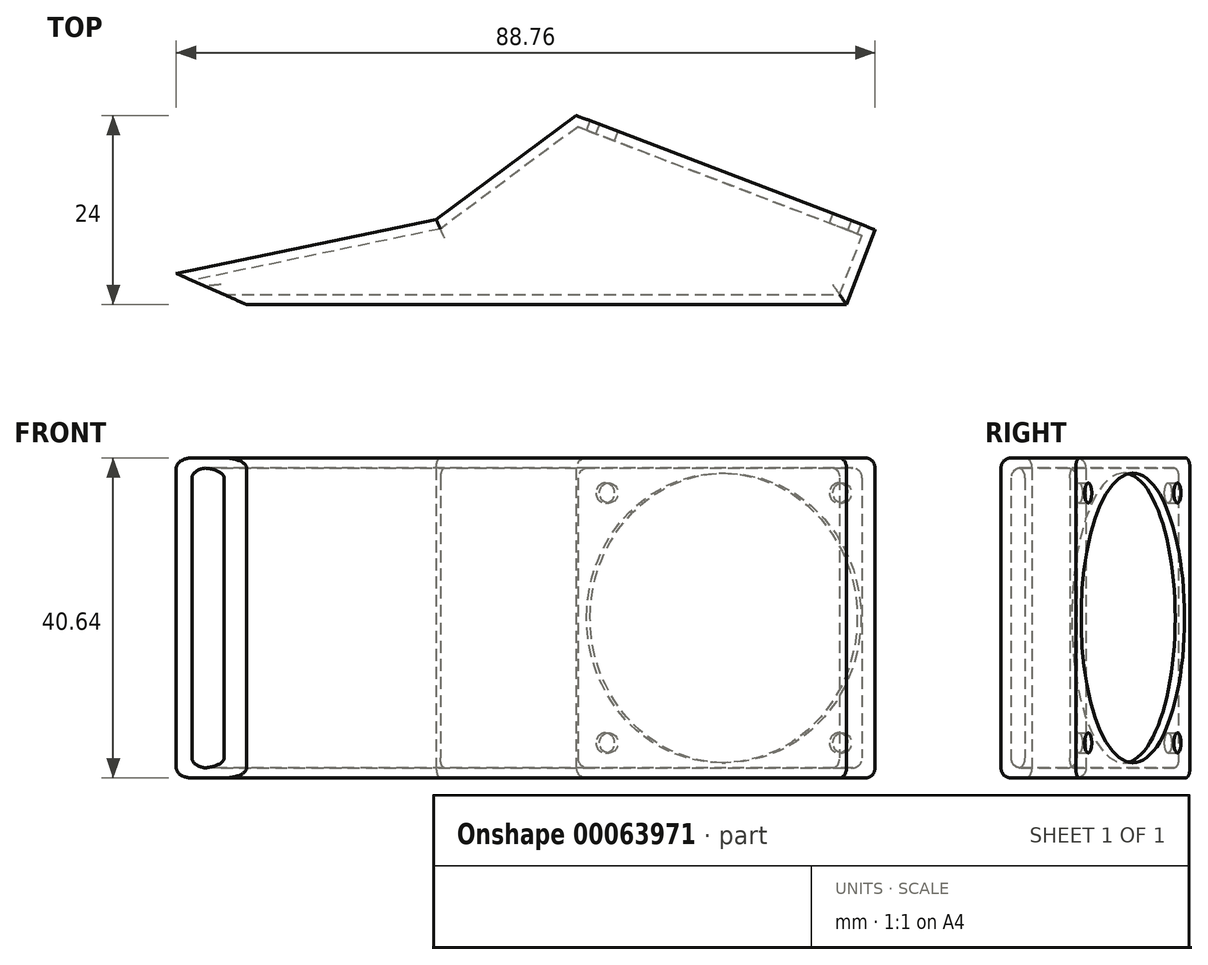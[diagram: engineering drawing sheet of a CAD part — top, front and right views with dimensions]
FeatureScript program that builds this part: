
annotation { "Feature Type Name" : "Feature", "Feature Type Description" : "" }
export const myFeature = defineFeature(function(context is Context, id is Id, definition is map)
    precondition{}
    {
        {
            var Q0;
            Q0=qCreatedBy(makeId("Top.planeOp"),FACE);
            var sketch = newSketch(context, id + "F0", { "sketchPlane" : qUnion([Q0])});
            skLineSegment(sketch, "E0", {"start": v(-24.09, -10.8) * mm, "end": v(52.11, -10.8) * mm});
            skLineSegment(sketch, "E1", {"start": v(52.11, -10.8) * mm, "end": v(55.74, -1.31) * mm});
            skLineSegment(sketch, "E2", {"start": v(55.74, -1.31) * mm, "end": v(17.78, 13.2) * mm});
            skLineSegment(sketch, "E3", {"start": v(17.78, 13.2) * mm, "end": v(0, 0) * mm});
            skLineSegment(sketch, "E4", {"start": v(0, 0) * mm, "end": v(-33.02, -6.85) * mm});
            skLineSegment(sketch, "E5", {"start": v(-33.02, -6.85) * mm, "end": v(-24.09, -10.8) * mm});
            skSolve(sketch);
        }
        {
            var Q0;
            Q0=makeQuery(id+"F0.imprint","IMPRINT",FACE,{"disambiguationData":[TD([[makeQuery(id+"F0.imprint","IMPRINT",EDGE,{"derivedFrom":sQuery(id+"F0.wireOp",EDGE,"E0")}),1.0]])]});
            extrude(context, id + "F1", {"entities" : qUnion([Q0]), "depth" : 40.64 * mm});
        }
        {
            var Q0;
            Q0=makeQuery(id+"F1.opExtrude","SWEPT_FACE",FACE,{"disambiguationData":[OSD([sQuery(id+"F0.wireOp",EDGE,"E2")])]});
            var sketch = newSketch(context, id + "F2", { "sketchPlane" : qUnion([Q0])});
            skCircle(sketch, "E6", {"center": v(-32.21, 20.32) * mm, "radius": 18.41 * mm});
            skSolve(sketch);
        }
        {
            var Q0;
            Q0=makeQuery(id+"F2.imprint","IMPRINT",FACE,{"disambiguationData":[TD([[makeQuery(id+"F2.imprint","IMPRINT",EDGE,{"derivedFrom":sQuery(id+"F2.wireOp",EDGE,"E6")}),1.0]])]});
            extrude(context, id + "F3", {"entities" : qUnion([Q0]), "operationType" : NewBodyOperationType.REMOVE, "oppositeDirection" : true, "depth" : 1.27 * mm});
        }
        {
            var Q0;
            Q0=makeQuery(id+"F3.boolean.opBoolean","COPY",FACE,{"derivedFrom":makeQuery(id+"F3.opExtrude","CAP_FACE",FACE,{"disambiguationData":[OSD([sQuery(id+"F2.wireOp",EDGE,"E6")])],"isStart":false})});
            var Q1;
            Q1=makeQuery(id+"F1.opExtrude","SWEPT_FACE",FACE,{"disambiguationData":[OSD([sQuery(id+"F0.wireOp",EDGE,"E5")])]});
            shell(context, id + "F4", {"entities" : qUnion([Q0, Q1]), "thickness" : 1.27 * mm});
        }
        {
            var Q0;
            Q0=makeQuery(id+"F1.opExtrude","SWEPT_FACE",FACE,{"disambiguationData":[OSD([sQuery(id+"F0.wireOp",EDGE,"E2")])]});
            var sketch = newSketch(context, id + "F5", { "sketchPlane" : qUnion([Q0])});
            skCircle(sketch, "E7", {"center": v(-48.09, 36.2) * mm, "radius": 1.27 * mm});
            skCircle(sketch, "E8", {"center": v(-16.34, 36.2) * mm, "radius": 1.27 * mm});
            skCircle(sketch, "E9", {"center": v(-16.34, 4.45) * mm, "radius": 1.27 * mm});
            skCircle(sketch, "E10", {"center": v(-48.09, 4.45) * mm, "radius": 1.27 * mm});
            skSolve(sketch);
        }
        {
            var Q0;
            Q0=sQuery(id+"F5.wireOp",VERTEX,"E7.center");
            var Q1;
            Q1=sQuery(id+"F5.wireOp",VERTEX,"E8.center");
            var Q2;
            Q2=sQuery(id+"F5.wireOp",VERTEX,"E9.center");
            var Q3;
            Q3=sQuery(id+"F5.wireOp",VERTEX,"E10.center");
            var Q4;
            Q4=makeQuery(id+"F1.opExtrude","SWEPT_BODY",BODY,{"disambiguationData":[OSD([sQuery(id+"F0.wireOp",EDGE,"E0"),sQuery(id+"F0.wireOp",EDGE,"E1"),sQuery(id+"F0.wireOp",EDGE,"E2"),sQuery(id+"F0.wireOp",EDGE,"E3"),sQuery(id+"F0.wireOp",EDGE,"E4"),sQuery(id+"F0.wireOp",EDGE,"E5")])]});
            hole(context, id + "F6", {"style" : HoleStyle.SIMPLE, "holeDiameter" : 2.54 * mm, "endStyle" : HoleEndStyle.BLIND, "holeDepth" : 8.9 * mm, "locations" : qUnion([Q0, Q1, Q2, Q3]), "scope" : qUnion([Q4])});
        }
        {
            var Q0;
            {var subQ0=sQuery(id+"F0.wireOp",EDGE,"E1");Q0=makeQuery(id+"F4.opShell","OFFSET_EDGE",EDGE,{"disambiguationData":[OSD([subQ0]),TDD([makeQuery(id+"F1.opExtrude","CAP_EDGE",EDGE,{"disambiguationData":[OSD([subQ0])],"isStart":false})])]});}
            var Q1;
            Q1=makeQuery(id+"F1.opExtrude","CAP_EDGE",EDGE,{"disambiguationData":[OSD([sQuery(id+"F0.wireOp",EDGE,"E1")])],"isStart":false});
            var Q2;
            {var subQ0=sQuery(id+"F0.wireOp",EDGE,"E3");Q2=makeQuery(id+"F4.opShell","OFFSET_EDGE",EDGE,{"disambiguationData":[OSD([subQ0]),TDD([makeQuery(id+"F1.opExtrude","CAP_EDGE",EDGE,{"disambiguationData":[OSD([subQ0])],"isStart":true})])]});}
            var Q3;
            Q3=makeQuery(id+"F1.opExtrude","CAP_EDGE",EDGE,{"disambiguationData":[OSD([sQuery(id+"F0.wireOp",EDGE,"E3")])],"isStart":true});
            var Q4;
            {var subQ0=sQuery(id+"F0.wireOp",EDGE,"E3");Q4=makeQuery(id+"F4.opShell","OFFSET_EDGE",EDGE,{"disambiguationData":[OSD([subQ0]),TDD([makeQuery(id+"F1.opExtrude","CAP_EDGE",EDGE,{"disambiguationData":[OSD([subQ0])],"isStart":false})])]});}
            var Q5;
            Q5=makeQuery(id+"F1.opExtrude","CAP_EDGE",EDGE,{"disambiguationData":[OSD([sQuery(id+"F0.wireOp",EDGE,"E3")])],"isStart":false});
            var Q6;
            {var subQ0=sQuery(id+"F0.wireOp",EDGE,"E4");Q6=makeQuery(id+"F4.opShell","OFFSET_EDGE",EDGE,{"disambiguationData":[OSD([subQ0]),TDD([makeQuery(id+"F1.opExtrude","CAP_EDGE",EDGE,{"disambiguationData":[OSD([subQ0])],"isStart":false})])]});}
            var Q7;
            Q7=makeQuery(id+"F1.opExtrude","CAP_EDGE",EDGE,{"disambiguationData":[OSD([sQuery(id+"F0.wireOp",EDGE,"E4")])],"isStart":false});
            var Q8;
            {var subQ0=sQuery(id+"F0.wireOp",EDGE,"E4");Q8=makeQuery(id+"F4.opShell","OFFSET_EDGE",EDGE,{"disambiguationData":[OSD([subQ0]),TDD([makeQuery(id+"F1.opExtrude","CAP_EDGE",EDGE,{"disambiguationData":[OSD([subQ0])],"isStart":true})])]});}
            var Q9;
            Q9=makeQuery(id+"F1.opExtrude","CAP_EDGE",EDGE,{"disambiguationData":[OSD([sQuery(id+"F0.wireOp",EDGE,"E4")])],"isStart":true});
            var Q10;
            {var subQ0=sQuery(id+"F0.wireOp",EDGE,"E1");Q10=makeQuery(id+"F4.opShell","OFFSET_EDGE",EDGE,{"disambiguationData":[OSD([subQ0]),TDD([makeQuery(id+"F1.opExtrude","CAP_EDGE",EDGE,{"disambiguationData":[OSD([subQ0])],"isStart":true})])]});}
            var Q11;
            Q11=makeQuery(id+"F1.opExtrude","CAP_EDGE",EDGE,{"disambiguationData":[OSD([sQuery(id+"F0.wireOp",EDGE,"E1")])],"isStart":true});
            var Q12;
            {var subQ0=sQuery(id+"F0.wireOp",EDGE,"E0");Q12=makeQuery(id+"F4.opShell","OFFSET_EDGE",EDGE,{"disambiguationData":[OSD([subQ0]),TDD([makeQuery(id+"F1.opExtrude","CAP_EDGE",EDGE,{"disambiguationData":[OSD([subQ0])],"isStart":true})])]});}
            var Q13;
            Q13=makeQuery(id+"F1.opExtrude","CAP_EDGE",EDGE,{"disambiguationData":[OSD([sQuery(id+"F0.wireOp",EDGE,"E0")])],"isStart":true});
            var Q14;
            {var subQ0=sQuery(id+"F0.wireOp",EDGE,"E0");Q14=makeQuery(id+"F4.opShell","OFFSET_EDGE",EDGE,{"disambiguationData":[OSD([subQ0]),TDD([makeQuery(id+"F1.opExtrude","CAP_EDGE",EDGE,{"disambiguationData":[OSD([subQ0])],"isStart":false})])]});}
            var Q15;
            Q15=makeQuery(id+"F1.opExtrude","CAP_EDGE",EDGE,{"disambiguationData":[OSD([sQuery(id+"F0.wireOp",EDGE,"E0")])],"isStart":false});
            fillet(context, id + "F7", {"entities" : qUnion([Q0, Q1, Q2, Q3, Q4, Q5, Q6, Q7, Q8, Q9, Q10, Q11, Q12, Q13, Q14, Q15]), "radius" : 1.27 * mm, "tangentPropagation" : true, "allowEdgeOverflow" : false});
        }
        {
            var Q0;
            Q0=qCreatedBy(makeId("Front.planeOp"),FACE);
            var sketch = newSketch(context, id + "F8", { "sketchPlane" : qUnion([Q0])});
            skLineSegment(sketch, "E11.bottom", {"start": v(-54.73, 199.04) * mm, "end": v(-48.38, 199.04) * mm});
            skLineSegment(sketch, "E11.top", {"start": v(-54.73, 190.15) * mm, "end": v(-48.38, 190.15) * mm});
            skLineSegment(sketch, "E11.left", {"start": v(-54.73, 199.04) * mm, "end": v(-54.73, 190.15) * mm});
            skLineSegment(sketch, "E11.right", {"start": v(-48.38, 199.04) * mm, "end": v(-48.38, 190.15) * mm});
            skSolve(sketch);
        }
        {
            var Q0;
            Q0 = qSketchRegion(id + "F8", true);
            extrude(context, id + "F9", {"entities" : qUnion([Q0]), "depth" : 25.4 * mm});
        }
        {
            var Q0;
            Q0=makeQuery(id+"F9.opExtrude","SWEPT_FACE",FACE,{"disambiguationData":[OSD([sQuery(id+"F8.wireOp",EDGE,"E11.right")])]});
            var sketch = newSketch(context, id + "F10", { "sketchPlane" : qUnion([Q0])});
            skLineSegment(sketch, "E12.bottom", {"start": v(-22.23, 196.18) * mm, "end": v(-3.18, 196.18) * mm});
            skLineSegment(sketch, "E12.top", {"start": v(-22.23, 193) * mm, "end": v(-3.18, 193) * mm});
            skLineSegment(sketch, "E12.left", {"start": v(-22.23, 196.18) * mm, "end": v(-22.23, 193) * mm});
            skLineSegment(sketch, "E12.right", {"start": v(-3.18, 196.18) * mm, "end": v(-3.18, 193) * mm});
            skSolve(sketch);
        }
        {
            var Q0;
            Q0 = qSketchRegion(id + "F10", true);
            extrude(context, id + "F11", {"entities" : qUnion([Q0]), "operationType" : NewBodyOperationType.REMOVE, "oppositeDirection" : true, "depth" : 25.4 * mm});
        }
        {
            var Q0;
            Q0=makeQuery(id+"F9.opExtrude","CAP_EDGE",EDGE,{"disambiguationData":[OSD([sQuery(id+"F8.wireOp",EDGE,"E11.bottom")])],"isStart":false});
            var Q1;
            Q1=makeQuery(id+"F9.opExtrude","CAP_EDGE",EDGE,{"disambiguationData":[OSD([sQuery(id+"F8.wireOp",EDGE,"E11.top")])],"isStart":false});
            var Q2;
            Q2=makeQuery(id+"F9.opExtrude","CAP_EDGE",EDGE,{"disambiguationData":[OSD([sQuery(id+"F8.wireOp",EDGE,"E11.bottom")])],"isStart":true});
            var Q3;
            Q3=makeQuery(id+"F9.opExtrude","CAP_EDGE",EDGE,{"disambiguationData":[OSD([sQuery(id+"F8.wireOp",EDGE,"E11.top")])],"isStart":true});
            var Q4;
            Q4=makeQuery(id+"F11.boolean.opBoolean","COPY",EDGE,{"derivedFrom":makeQuery(id+"F11.opExtrude","SWEPT_EDGE",EDGE,{"disambiguationData":[OSD([sQuery(id+"F10.wireOp",EDGE,"E12.bottom"),sQuery(id+"F10.wireOp",EDGE,"E12.left")])]})});
            var Q5;
            Q5=makeQuery(id+"F11.boolean.opBoolean","COPY",EDGE,{"derivedFrom":makeQuery(id+"F11.opExtrude","SWEPT_EDGE",EDGE,{"disambiguationData":[OSD([sQuery(id+"F10.wireOp",EDGE,"E12.top"),sQuery(id+"F10.wireOp",EDGE,"E12.left")])]})});
            var Q6;
            Q6=makeQuery(id+"F11.boolean.opBoolean","COPY",EDGE,{"derivedFrom":makeQuery(id+"F11.opExtrude","SWEPT_EDGE",EDGE,{"disambiguationData":[OSD([sQuery(id+"F10.wireOp",EDGE,"E12.top"),sQuery(id+"F10.wireOp",EDGE,"E12.right")])]})});
            var Q7;
            Q7=makeQuery(id+"F11.boolean.opBoolean","COPY",EDGE,{"derivedFrom":makeQuery(id+"F11.opExtrude","SWEPT_EDGE",EDGE,{"disambiguationData":[OSD([sQuery(id+"F10.wireOp",EDGE,"E12.bottom"),sQuery(id+"F10.wireOp",EDGE,"E12.right")])]})});
            fillet(context, id + "F12", {"entities" : qUnion([Q0, Q1, Q2, Q3, Q4, Q5, Q6, Q7]), "radius" : 1.27 * mm, "tangentPropagation" : true, "allowEdgeOverflow" : false});
        }
        {
            var Q0;
            Q0=makeQuery(id+"F9.opExtrude","SWEPT_BODY",BODY,{"disambiguationData":[OSD([sQuery(id+"F8.wireOp",EDGE,"E11.bottom"),sQuery(id+"F8.wireOp",EDGE,"E11.top"),sQuery(id+"F8.wireOp",EDGE,"E11.left"),sQuery(id+"F8.wireOp",EDGE,"E11.right")])]});
            deleteBodies(context, id + "F13", {"entities" : qUnion([Q0])});
        }
    });
